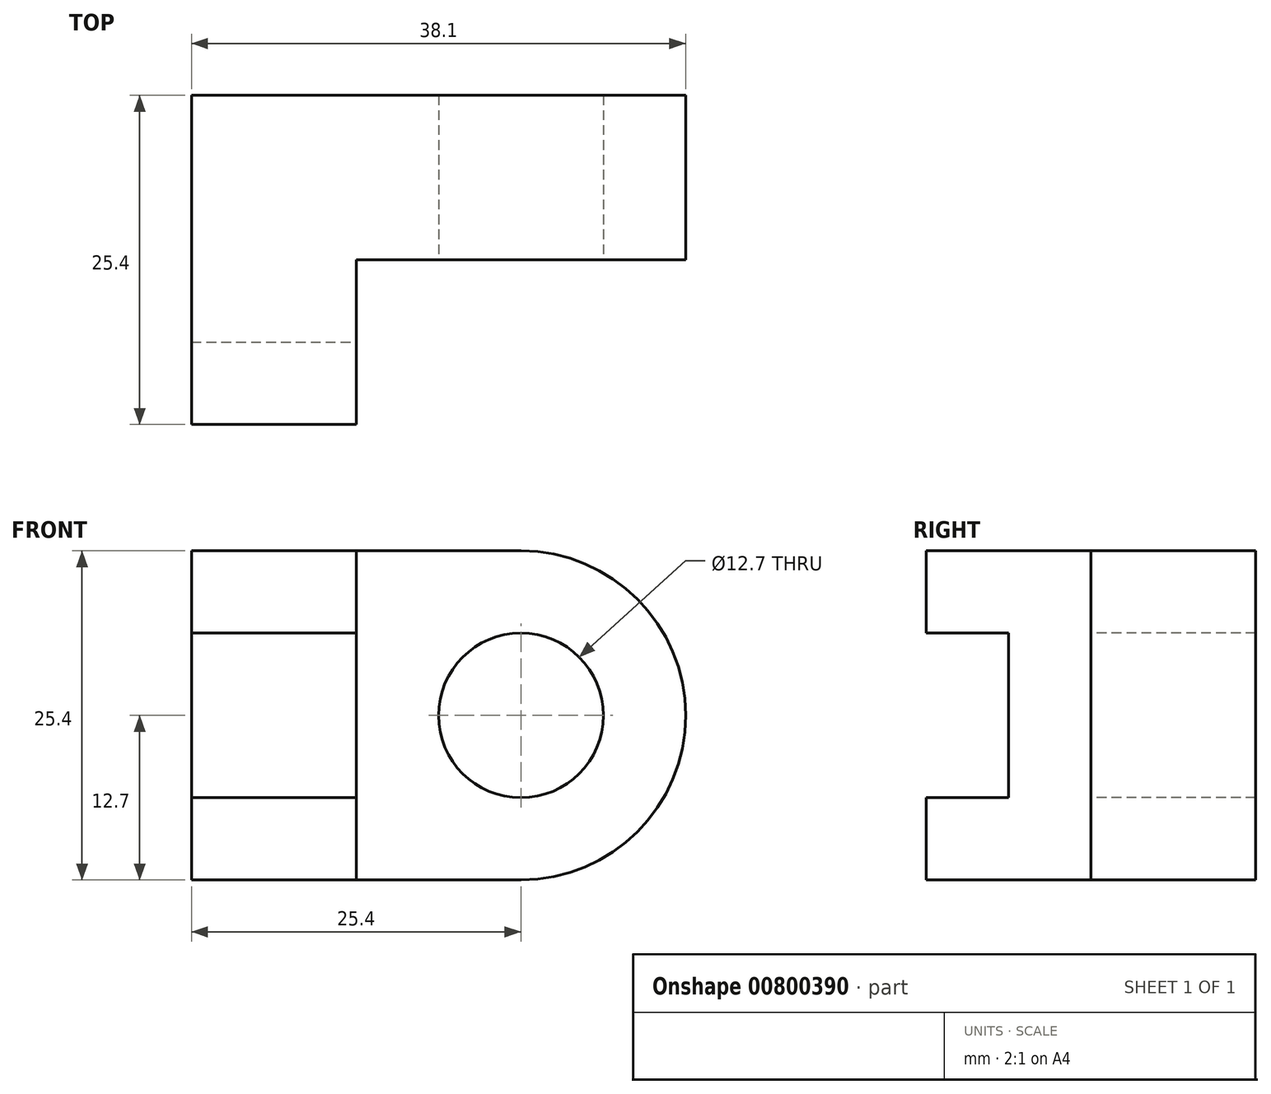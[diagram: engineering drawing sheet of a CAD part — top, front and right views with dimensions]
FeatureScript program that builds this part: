
annotation { "Feature Type Name" : "Feature", "Feature Type Description" : "" }
export const myFeature = defineFeature(function(context is Context, id is Id, definition is map)
    precondition{}
    {
        {
            var Q0;
            Q0=qCreatedBy(makeId("Front.planeOp"),FACE);
            var sketch = newSketch(context, id + "F0", { "sketchPlane" : qUnion([Q0])});
            skLineSegment(sketch, "E0", {"start": v(0, 0) * mm, "end": v(12.7, 0) * mm});
            skLineSegment(sketch, "E1", {"start": v(12.7, 0) * mm, "end": v(12.7, 25.4) * mm});
            skLineSegment(sketch, "E2", {"start": v(12.7, 25.4) * mm, "end": v(0, 25.4) * mm});
            skLineSegment(sketch, "E3", {"start": v(0, 25.4) * mm, "end": v(0, 0) * mm});
            skSolve(sketch);
        }
        {
            var Q0;
            Q0=makeQuery(id+"F0.imprint","IMPRINT",FACE,{"disambiguationData":[TD([[makeQuery(id+"F0.imprint","IMPRINT",EDGE,{"derivedFrom":sQuery(id+"F0.wireOp",EDGE,"E0")}),1.0]])]});
            extrude(context, id + "F1", {"entities" : qUnion([Q0]), "depth" : 25.4 * mm, "offsetDistance" : 25.4 * mm});
        }
        {
            var Q0;
            Q0=makeQuery(id+"F1.opExtrude","SWEPT_FACE",FACE,{"disambiguationData":[OSD([sQuery(id+"F0.wireOp",EDGE,"E1")])]});
            var sketch = newSketch(context, id + "F2", { "sketchPlane" : qUnion([Q0])});
            skLineSegment(sketch, "E4", {"start": v(-25.4, 25.4) * mm, "end": v(-25.4, 19.05) * mm});
            skLineSegment(sketch, "E5", {"start": v(-25.4, 19.05) * mm, "end": v(-19.05, 19.05) * mm});
            skLineSegment(sketch, "E6", {"start": v(-19.05, 19.05) * mm, "end": v(-19.05, 6.35) * mm});
            skLineSegment(sketch, "E7", {"start": v(-19.05, 6.35) * mm, "end": v(-25.4, 6.35) * mm});
            skSolve(sketch);
        }
        {
            var Q0;
            {var subQ0=sQuery(id+"F2.wireOp",EDGE,"E5");Q0=makeQuery(id+"F2.imprint","IMPRINT",FACE,{"disambiguationData":[TD([[makeQuery(id+"F2.imprint","IMPRINT",EDGE,{"derivedFrom":subQ0}),-1.0]])]});}
            extrude(context, id + "F3", {"entities" : qUnion([Q0]), "operationType" : NewBodyOperationType.REMOVE, "oppositeDirection" : true, "depth" : 25.4 * mm, "offsetDistance" : 25.4 * mm});
        }
        {
            var Q0;
            Q0=makeQuery(id+"F1.opExtrude","SWEPT_FACE",FACE,{"disambiguationData":[OSD([sQuery(id+"F0.wireOp",EDGE,"E1")])]});
            var sketch = newSketch(context, id + "F4", { "sketchPlane" : qUnion([Q0])});
            skLineSegment(sketch, "E8", {"start": v(0, 25.4) * mm, "end": v(-12.7, 25.4) * mm});
            skLineSegment(sketch, "E9", {"start": v(-12.7, 25.4) * mm, "end": v(-12.7, 0) * mm});
            skSolve(sketch);
        }
        {
            var Q0;
            Q0=makeQuery(id+"F4.imprint","IMPRINT",FACE,{"disambiguationData":[TD([[makeQuery(id+"F4.imprint","IMPRINT",EDGE,{"derivedFrom":sQuery(id+"F4.wireOp",EDGE,"E8")}),-1.0]])]});
            extrude(context, id + "F5", {"entities" : qUnion([Q0]), "operationType" : NewBodyOperationType.ADD, "depth" : 25.4 * mm, "offsetDistance" : 25.4 * mm});
        }
        {
            var Q0;
            Q0=makeQuery(id+"F5.opExtrude","SWEPT_FACE",FACE,{"disambiguationData":[OSD([sQuery(id+"F4.wireOp",EDGE,"E9")])]});
            var sketch = newSketch(context, id + "F6", { "sketchPlane" : qUnion([Q0])});
            skArc(sketch, "E10", {"start": v(25.4, 0) * mm, "mid": v(38.1, 12.7) * mm, "end": v(25.4, 25.4) * mm});
            skSolve(sketch);
        }
        {
            var Q0;
            {var subQ0=sQuery(id+"F6.wireOp",EDGE,"E10");var subQ1=sQuery(id+"F4.wireOp",EDGE,"E9");var subQ4=makeQuery(id+"F5.opExtrude","CAP_EDGE",EDGE,{"disambiguationData":[OSD([subQ1])],"isStart":false});var subQ5=makeQuery(id+"F6.imprint","INTERSECT",VERTEX,{"derivedFrom":[subQ4,subQ0]});Q0=makeQuery(id+"F6.imprint","IMPRINT",FACE,{"disambiguationData":[TD([[makeQuery(id+"F6.imprint","IMPRINT",EDGE,{"disambiguationData":[TD([[subQ5,-1.0]])],"derivedFrom":subQ0}),-1.0]])]});}
            var Q1;
            {var subQ0=sQuery(id+"F6.wireOp",EDGE,"E10");var subQ1=sQuery(id+"F4.wireOp",EDGE,"E9");var subQ4=makeQuery(id+"F5.opExtrude","CAP_EDGE",EDGE,{"disambiguationData":[OSD([subQ1])],"isStart":false});var subQ5=makeQuery(id+"F6.imprint","INTERSECT",VERTEX,{"derivedFrom":[subQ4,subQ0]});Q1=makeQuery(id+"F6.imprint","IMPRINT",FACE,{"disambiguationData":[TD([[makeQuery(id+"F6.imprint","IMPRINT",EDGE,{"disambiguationData":[TD([[subQ5,1.0]])],"derivedFrom":subQ0}),-1.0]])]});}
            extrude(context, id + "F7", {"entities" : qUnion([Q0, Q1]), "operationType" : NewBodyOperationType.REMOVE, "oppositeDirection" : true, "depth" : 25.4 * mm, "offsetDistance" : 25.4 * mm});
        }
        {
            var Q0;
            Q0=makeQuery(id+"F5.opExtrude","SWEPT_FACE",FACE,{"disambiguationData":[OSD([sQuery(id+"F4.wireOp",EDGE,"E9")])]});
            var sketch = newSketch(context, id + "F8", { "sketchPlane" : qUnion([Q0])});
            skLineSegment(sketch, "E11", {"start": v(12.7, 12.7) * mm, "end": v(19.05, 12.7) * mm, "construction": true});
            skLineSegment(sketch, "E12", {"start": v(19.05, 12.7) * mm, "end": v(31.75, 12.7) * mm, "construction": true});
            skCircle(sketch, "E13", {"center": v(25.4, 12.7) * mm, "radius": 6.35 * mm});
            skSolve(sketch);
        }
        {
            var Q0;
            Q0=makeQuery(id+"F8.imprint","IMPRINT",FACE,{"disambiguationData":[TD([[makeQuery(id+"F8.imprint","IMPRINT",EDGE,{"derivedFrom":sQuery(id+"F8.wireOp",EDGE,"E13")}),1.0]])]});
            extrude(context, id + "F9", {"entities" : qUnion([Q0]), "operationType" : NewBodyOperationType.REMOVE, "oppositeDirection" : true, "depth" : 25.4 * mm, "offsetDistance" : 25.4 * mm});
        }
    });
